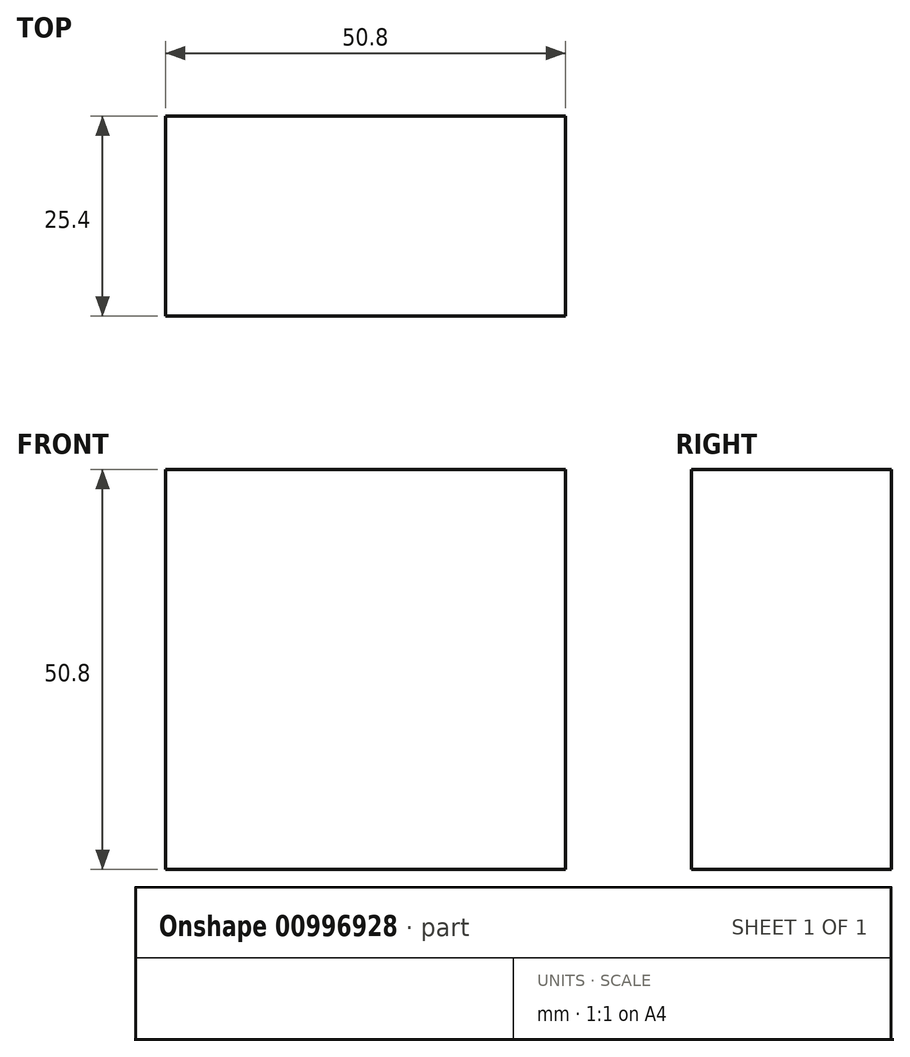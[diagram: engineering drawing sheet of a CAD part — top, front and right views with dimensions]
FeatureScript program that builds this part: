
annotation { "Feature Type Name" : "Feature", "Feature Type Description" : "" }
export const myFeature = defineFeature(function(context is Context, id is Id, definition is map)
    precondition{}
    {
        {
            var Q0;
            Q0=qCreatedBy(makeId("Front.planeOp"),FACE);
            var sketch = newSketch(context, id + "F0", { "sketchPlane" : qUnion([Q0])});
            skLineSegment(sketch, "E0.bottom", {"start": v(0, 0) * mm, "end": v(50.8, 0) * mm});
            skLineSegment(sketch, "E0.top", {"start": v(0, 50.8) * mm, "end": v(50.8, 50.8) * mm});
            skLineSegment(sketch, "E0.left", {"start": v(0, 0) * mm, "end": v(0, 50.8) * mm});
            skLineSegment(sketch, "E0.right", {"start": v(50.8, 0) * mm, "end": v(50.8, 50.8) * mm});
            skSolve(sketch);
        }
        {
            var Q0;
            Q0 = qSketchRegion(id + "F0", true);
            extrude(context, id + "F1", {"entities" : qUnion([Q0]), "depth" : 25.4 * mm, "offsetDistance" : 25.4 * mm});
        }
    });
